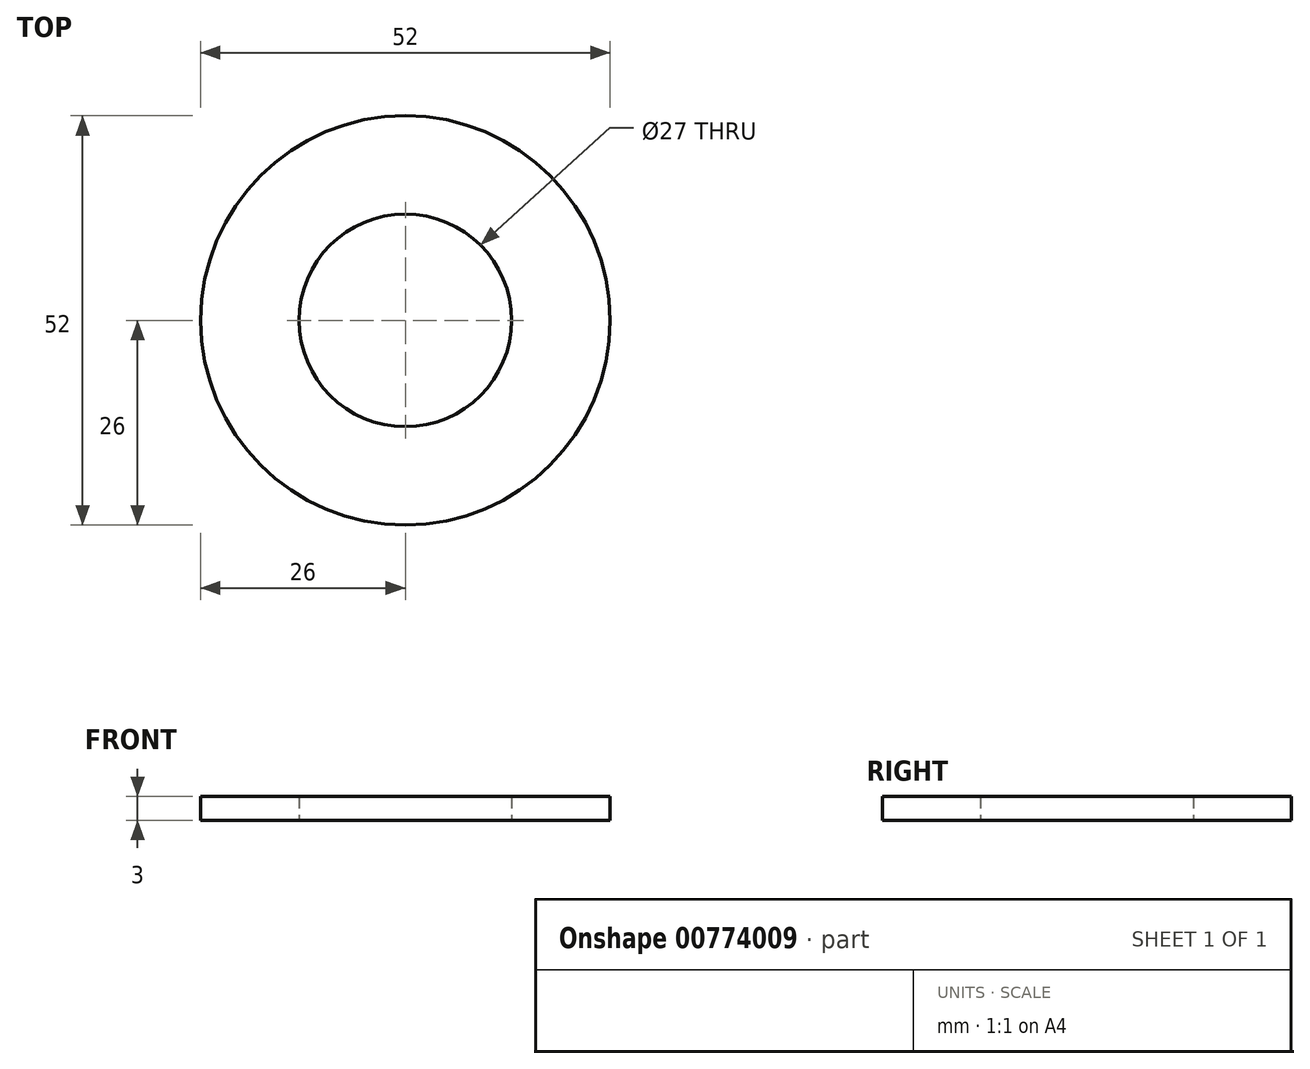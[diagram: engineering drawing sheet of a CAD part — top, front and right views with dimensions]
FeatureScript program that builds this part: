
annotation { "Feature Type Name" : "Feature", "Feature Type Description" : "" }
export const myFeature = defineFeature(function(context is Context, id is Id, definition is map)
    precondition{}
    {
        {
            var Q0;
            Q0=qCreatedBy(makeId("Top.planeOp"),FACE);
            var sketch = newSketch(context, id + "F0", { "sketchPlane" : qUnion([Q0])});
            skCircle(sketch, "E0", {"center": v(0, 0) * mm, "radius": 26 * mm});
            skCircle(sketch, "E1", {"center": v(0, 0) * mm, "radius": 13.5 * mm});
            skSolve(sketch);
        }
        {
            var Q0;
            Q0 = qSketchRegion(id + "F0", true);
            extrude(context, id + "F1", {"entities" : qUnion([Q0]), "depth" : 3 * mm, "offsetDistance" : 25 * mm, "symmetric" : true});
        }
    });
